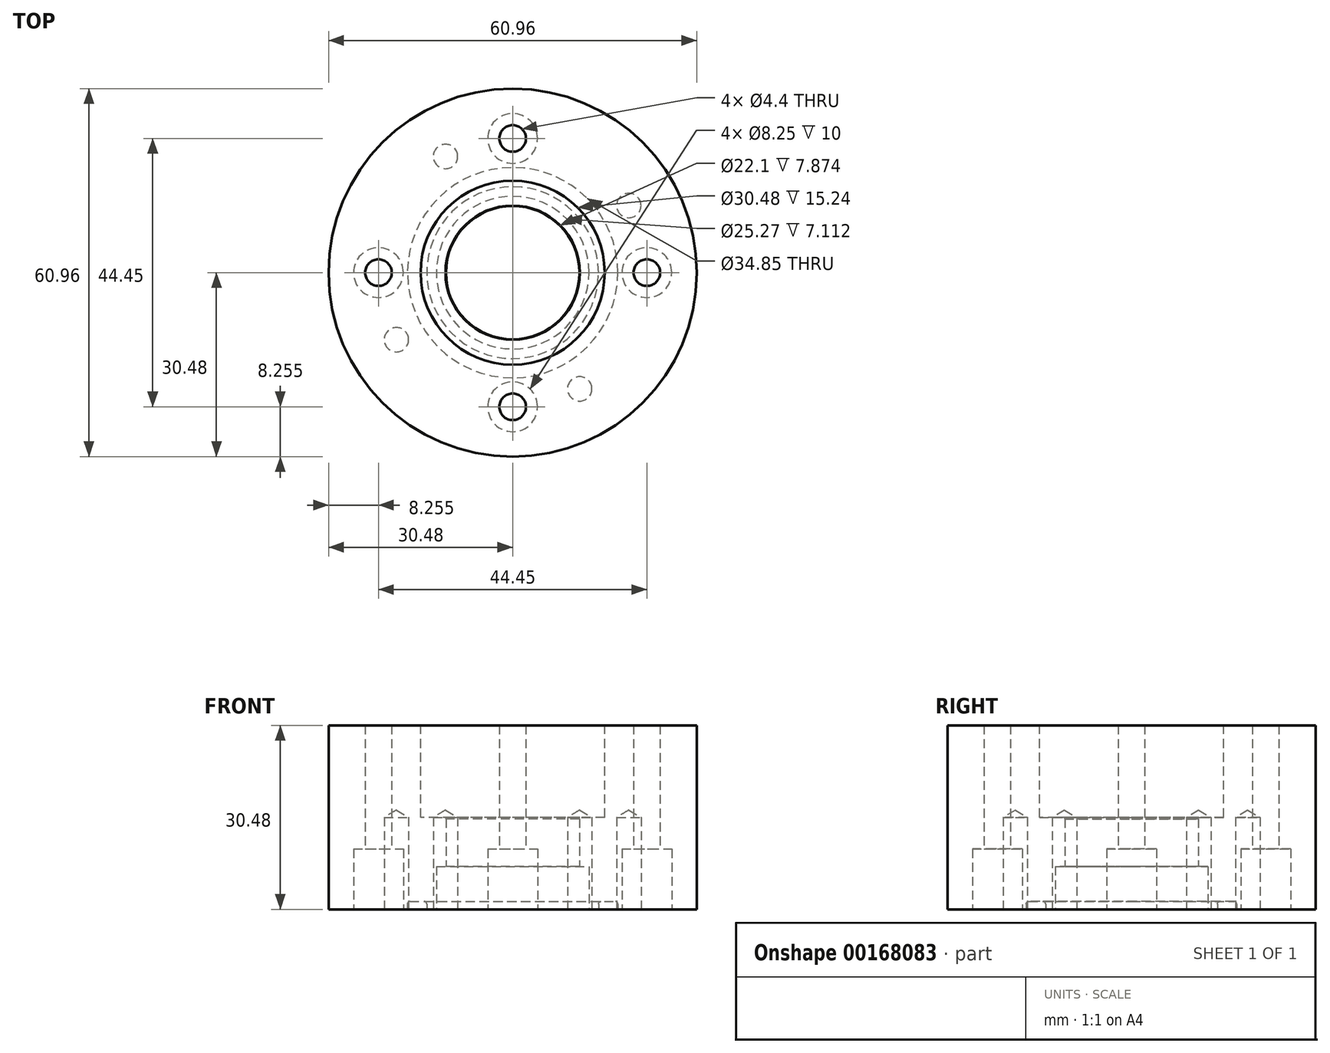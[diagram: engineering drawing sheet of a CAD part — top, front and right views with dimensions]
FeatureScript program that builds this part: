
annotation { "Feature Type Name" : "Feature", "Feature Type Description" : "" }
export const myFeature = defineFeature(function(context is Context, id is Id, definition is map)
    precondition{}
    {
        {
            var Q0;
            Q0=qCreatedBy(makeId("Top.planeOp"),FACE);
            var sketch = newSketch(context, id + "F0", { "sketchPlane" : qUnion([Q0])});
            skCircle(sketch, "E0", {"center": v(0, 0) * mm, "radius": 30.48 * mm});
            skCircle(sketch, "E1", {"center": v(0, 0) * mm, "radius": 11.05 * mm});
            skSolve(sketch);
        }
        {
            var Q0;
            Q0=qSketchRegion(id+"F0",true);
            extrude(context, id + "F1", {"entities" : qUnion([Q0]), "depth" : 30.48 * mm});
        }
        {
            var Q0;
            Q0=makeQuery(id+"F1.opExtrude","CAP_FACE",FACE,{"disambiguationData":[OSD([sQuery(id+"F0.wireOp",EDGE,"E0"),sQuery(id+"F0.wireOp",EDGE,"E1")])],"isStart":false});
            var sketch = newSketch(context, id + "F2", { "sketchPlane" : qUnion([Q0])});
            skCircle(sketch, "E2", {"center": v(0, 0) * mm, "radius": 15.24 * mm});
            skSolve(sketch);
        }
        {
            var Q0;
            Q0=qSketchRegion(id+"F2",true);
            extrude(context, id + "F3", {"entities" : qUnion([Q0]), "operationType" : NewBodyOperationType.REMOVE, "oppositeDirection" : true, "depth" : 15.24 * mm});
        }
        {
            var Q0;
            Q0=makeQuery(id+"F1.opExtrude","CAP_FACE",FACE,{"disambiguationData":[OSD([sQuery(id+"F0.wireOp",EDGE,"E0"),sQuery(id+"F0.wireOp",EDGE,"E1")])],"isStart":true});
            var sketch = newSketch(context, id + "F4", { "sketchPlane" : qUnion([Q0])});
            skCircle(sketch, "E3", {"center": v(0, 0) * mm, "radius": 12.64 * mm});
            skCircle(sketch, "E4.0", {"center": v(0, 0) * mm, "radius": 11.05 * mm});
            skSolve(sketch);
        }
        {
            var Q0;
            Q0=qSketchRegion(id+"F4",true);
            extrude(context, id + "F5", {"entities" : qUnion([Q0]), "operationType" : NewBodyOperationType.REMOVE, "oppositeDirection" : true, "depth" : 7.11 * mm});
        }
        {
            var Q0;
            Q0=makeQuery(id+"F3.boolean.opBoolean","INTERSECT",EDGE,{"derivedFrom":[makeQuery(id+"F1.opExtrude","SWEPT_FACE",FACE,{"disambiguationData":[OSD([sQuery(id+"F0.wireOp",EDGE,"E1")])]}),makeQuery(id+"F3.opExtrude","CAP_FACE",FACE,{"disambiguationData":[OSD([sQuery(id+"F2.wireOp",EDGE,"E2")])],"isStart":false})]});
            var Q1;
            Q1=makeQuery(id+"F5.boolean.opBoolean","COPY",EDGE,{"derivedFrom":makeQuery(id+"F5.opExtrude","CAP_EDGE",EDGE,{"disambiguationData":[OSD([sQuery(id+"F4.wireOp",EDGE,"E3")])],"isStart":true})});
            var Q2;
            Q2=makeQuery(id+"F5.boolean.opBoolean","COPY",EDGE,{"derivedFrom":makeQuery(id+"F5.opExtrude","CAP_EDGE",EDGE,{"disambiguationData":[OSD([sQuery(id+"F4.wireOp",EDGE,"E4.0")])],"isStart":false})});
            chamfer(context, id + "F6", {"entities" : qUnion([Q0, Q1, Q2]), "chamferType" : ChamferType.OFFSET_ANGLE, "width" : 0.25 * mm, "oppositeDirection" : false, "angle" : 15 * degree, "tangentPropagation" : true});
        }
        {
            var Q0;
            Q0=makeQuery(id+"F1.opExtrude","CAP_FACE",FACE,{"disambiguationData":[OSD([sQuery(id+"F0.wireOp",EDGE,"E0"),sQuery(id+"F0.wireOp",EDGE,"E1")])],"isStart":true});
            var sketch = newSketch(context, id + "F7", { "sketchPlane" : qUnion([Q0])});
            skPoint(sketch, "E5", {"position": v(0, -22.23) * mm});
            skPoint(sketch, "E6.1.0", {"position": v(22.23, 0) * mm});
            skPoint(sketch, "E6.2.0", {"position": v(0, 22.22) * mm});
            skPoint(sketch, "E6.3.0", {"position": v(-22.23, 0) * mm});
            skPoint(sketch, "E6.center", {"position": v(0, 0) * mm});
            skSolve(sketch);
        }
        {
            var Q0;
            Q0=sQuery(id+"F7.wireOp",VERTEX,"E5");
            var Q1;
            Q1=sQuery(id+"F7.wireOp",VERTEX,"E6.3.0");
            var Q2;
            Q2=sQuery(id+"F7.wireOp",VERTEX,"E6.2.0");
            var Q3;
            Q3=sQuery(id+"F7.wireOp",VERTEX,"E6.1.0");
            var Q4;
            Q4=makeQuery(id+"F1.opExtrude","SWEPT_BODY",BODY,{"disambiguationData":[OSD([sQuery(id+"F0.wireOp",EDGE,"E0"),sQuery(id+"F0.wireOp",EDGE,"E1")])]});
            hole(context, id + "F8", {"style" : HoleStyle.C_BORE, "endStyle" : HoleEndStyle.THROUGH, "holeDiameter" : 4.4 * mm, "cBoreDiameter" : 8.25 * mm, "cBoreDepth" : 10 * mm, "locations" : qUnion([Q0, Q1, Q2, Q3]), "scope" : qUnion([Q4]), "isTappedThrough" : true});
        }
        {
            var Q0;
            Q0=makeQuery(id+"F1.opExtrude","CAP_FACE",FACE,{"disambiguationData":[OSD([sQuery(id+"F0.wireOp",EDGE,"E0"),sQuery(id+"F0.wireOp",EDGE,"E1")])],"isStart":true});
            var sketch = newSketch(context, id + "F9", { "sketchPlane" : qUnion([Q0])});
            skLineSegment(sketch, "E7", {"start": v(0, 0) * mm, "end": v(-19.25, 11.11) * mm, "construction": true});
            skPoint(sketch, "E8", {"position": v(-19.25, 11.11) * mm});
            skPoint(sketch, "E9.1.0", {"position": v(-11.11, -19.25) * mm});
            skPoint(sketch, "E9.2.0", {"position": v(19.25, -11.11) * mm});
            skPoint(sketch, "E9.3.0", {"position": v(11.11, 19.25) * mm});
            skPoint(sketch, "E9.center", {"position": v(0, 0) * mm});
            skSolve(sketch);
        }
        {
            var Q0;
            Q0=sQuery(id+"F9.wireOp",VERTEX,"E8");
            var Q1;
            Q1=sQuery(id+"F9.wireOp",VERTEX,"E9.3.0");
            var Q2;
            Q2=sQuery(id+"F9.wireOp",VERTEX,"E9.2.0");
            var Q3;
            Q3=sQuery(id+"F9.wireOp",VERTEX,"E9.1.0");
            var Q4;
            Q4=makeQuery(id+"F1.opExtrude","SWEPT_BODY",BODY,{"disambiguationData":[OSD([sQuery(id+"F0.wireOp",EDGE,"E0"),sQuery(id+"F0.wireOp",EDGE,"E1")])]});
            hole(context, id + "F10", {"style" : HoleStyle.SIMPLE, "endStyle" : HoleEndStyle.BLIND, "standardTappedOrClearance" : lookupTablePath({ "standard" : "ANSI", "engagement" : "75%", "pitch" : "32 tpi", "size" : "#10", "type" : "Tapped" }), "standardBlindInLast" : lookupTablePath({ "standard" : "ANSI", "engagement" : "75%", "pitch" : "32 tpi", "size" : "#10", "type" : "Tapped" }), "holeDiameter" : 4.04 * mm, "holeDepth" : 15.24 * mm, "locations" : qUnion([Q0, Q1, Q2, Q3]), "scope" : qUnion([Q4]), "majorDiameter" : 4.83 * mm});
        }
        {
            var Q0;
            Q0=makeQuery(id+"F1.opExtrude","CAP_FACE",FACE,{"disambiguationData":[OSD([sQuery(id+"F0.wireOp",EDGE,"E0"),sQuery(id+"F0.wireOp",EDGE,"E1")])],"isStart":true});
            var sketch = newSketch(context, id + "F11", { "sketchPlane" : qUnion([Q0])});
            skCircle(sketch, "E10", {"center": v(0, 0) * mm, "radius": 14.22 * mm});
            skCircle(sketch, "E11", {"center": v(0, 0) * mm, "radius": 17.42 * mm});
            skCircle(sketch, "E12", {"center": v(0, 0) * mm, "radius": 15.82 * mm, "construction": true});
            skSolve(sketch);
        }
        {
            var Q0;
            Q0=qSketchRegion(id+"F11",true);
            extrude(context, id + "F12", {"entities" : qUnion([Q0]), "operationType" : NewBodyOperationType.REMOVE, "oppositeDirection" : true, "depth" : 1.3 * mm});
        }
        {
            var Q0;
            Q0=makeQuery(id+"F12.boolean.opBoolean","COPY",EDGE,{"derivedFrom":makeQuery(id+"F12.opExtrude","CAP_EDGE",EDGE,{"disambiguationData":[OSD([sQuery(id+"F11.wireOp",EDGE,"E10")])],"isStart":false})});
            var Q1;
            Q1=makeQuery(id+"F12.boolean.opBoolean","COPY",EDGE,{"derivedFrom":makeQuery(id+"F12.opExtrude","CAP_EDGE",EDGE,{"disambiguationData":[OSD([sQuery(id+"F11.wireOp",EDGE,"E11")])],"isStart":false})});
            fillet(context, id + "F13", {"entities" : qUnion([Q0, Q1]), "radius" : 0.4 * mm, "tangentPropagation" : true, "allowEdgeOverflow" : false});
        }
    });
